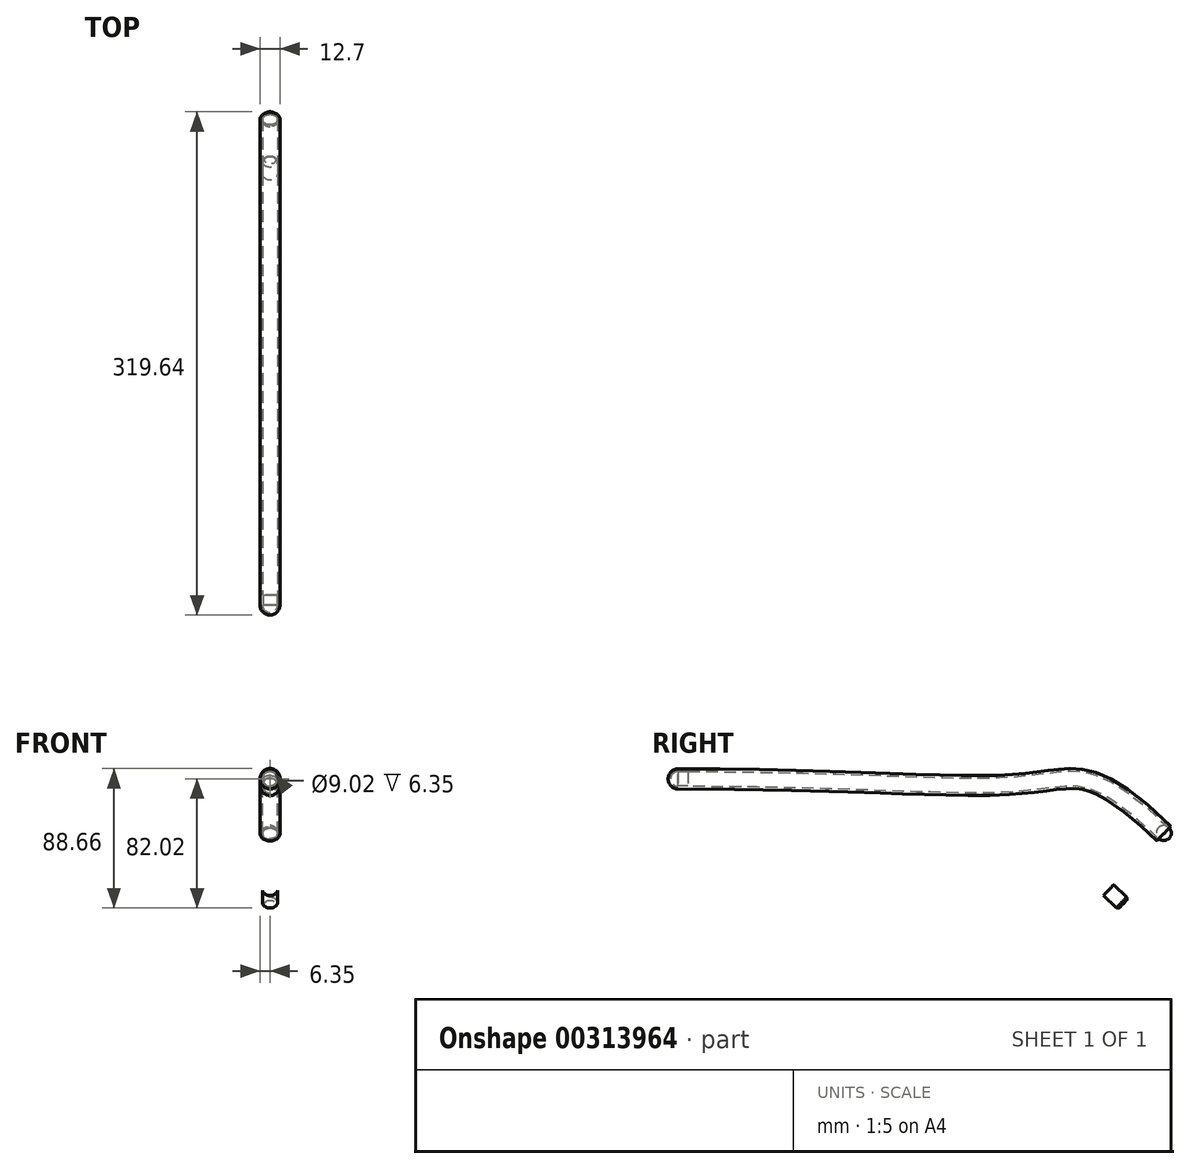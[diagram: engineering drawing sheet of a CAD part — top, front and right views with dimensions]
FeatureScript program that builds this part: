
annotation { "Feature Type Name" : "Feature", "Feature Type Description" : "" }
export const myFeature = defineFeature(function(context is Context, id is Id, definition is map)
    precondition{}
    {
        {
            var Q0;
            Q0=qCreatedBy(makeId("Right.planeOp"),FACE);
            var sketch = newSketch(context, id + "F0", { "sketchPlane" : qUnion([Q0])});
            skFitSpline(sketch, "E0", {"points": [v(-207.12, 0) * mm, v(0, -3.78) * mm, v(36.76, 0) * mm, v(101.4, -34.75) * mm], "startDerivative": vector(633.88, 0) * mm, "endDerivative": vector(361.52, -353.38) * mm});
            skPoint(sketch, "E1.0", {"position": v(0, 0) * mm});
            skFitSpline(sketch, "E2", {"points": [v(-207.12, 0) * mm, v(0, -3.78) * mm, v(36.76, 0) * mm, v(101.4, -34.75) * mm], "startDerivative": vector(633.88, 0) * mm, "endDerivative": vector(361.52, -353.38) * mm});
            skSolve(sketch);
        }
        {
            var Q0;
            Q0=sQuery(id+"F0.wireOp",VERTEX,"E0.start");
            var Q1;
            Q1=sQuery(id+"F0.wireOp",EDGE,"E0");
            cPlane(context, id + "F1", {"entities" : qUnion([Q0, Q1]), "cplaneType" : CPlaneType.CURVE_POINT, "offset" : 74.17 * mm, "width" : 152.4 * mm, "height" : 152.4 * mm});
        }
        {
            var Q0;
            Q0=qCreatedBy(makeId("Front.planeOp"),FACE);
            var Q1;
            Q1=sQuery(id+"F0.wireOp",VERTEX,"E0.3.internal");
            cPlane(context, id + "F2", {"entities" : qUnion([Q0, Q1]), "cplaneType" : CPlaneType.PLANE_POINT, "offset" : 76.2 * mm, "width" : 152.4 * mm, "height" : 152.4 * mm});
        }
        {
            var Q0;
            Q0=qCreatedBy(id+"F1.planeOp",FACE);
            var sketch = newSketch(context, id + "F3", { "sketchPlane" : qUnion([Q0])});
            skCircle(sketch, "E3", {"center": v(0, 0) * mm, "radius": 6.35 * mm});
            skCircle(sketch, "E4", {"center": v(0, 0) * mm, "radius": 4.76 * mm});
            skSolve(sketch);
        }
        {
            var Q0;
            Q0=qCreatedBy(id+"F2.planeOp",FACE);
            var sketch = newSketch(context, id + "F4", { "sketchPlane" : qUnion([Q0])});
            skArc(sketch, "E5", {"start": v(4.76, -34.23) * mm, "mid": v(-0.1, -29.56) * mm, "end": v(-4.76, -34.42) * mm});
            skLineSegment(sketch, "E6", {"start": v(4.76, -34.23) * mm, "end": v(-4.76, -34.42) * mm});
            skSolve(sketch);
        }
        {
            var Q0;
            Q0=makeQuery(id+"F3.imprint","IMPRINT",FACE,{"disambiguationData":[TD([[makeQuery(id+"F3.imprint","IMPRINT",EDGE,{"derivedFrom":sQuery(id+"F3.wireOp",EDGE,"E3")}),1.0]])]});
            var Q1;
            Q1 = qSketchRegion(id + "F0", true);
            var Q2;
            Q2=sQuery(id+"F0.wireOp",EDGE,"E0");
            sweep(context, id + "F5", {"profiles" : qUnion([Q0, Q1]), "path" : qUnion([Q2])});
        }
        {
            var Q0;
            Q0=makeQuery(id+"F5.opSweep","CAP_FACE",FACE,{"disambiguationData":[OSD([sQuery(id+"F0.wireOp",VERTEX,"E0.end"),sQuery(id+"F3.wireOp",EDGE,"E3"),sQuery(id+"F3.wireOp",EDGE,"E4")])],"isStart":false});
            var Q1;
            Q1=makeQuery(id+"F5.opSweep","CAP_FACE",FACE,{"disambiguationData":[OSD([sQuery(id+"F0.wireOp",VERTEX,"E0.end"),sQuery(id+"F3.wireOp",EDGE,"E3"),sQuery(id+"F3.wireOp",EDGE,"E4")])],"isStart":false});
            var Q2;
            Q2=makeQuery(id+"F5.opSweep","CAP_FACE",FACE,{"disambiguationData":[OSD([sQuery(id+"F0.wireOp",VERTEX,"E0.end"),sQuery(id+"F3.wireOp",EDGE,"E3"),sQuery(id+"F3.wireOp",EDGE,"E4")])],"isStart":false});
            var Q3;
            Q3=makeQuery(id+"F5.opSweep","CAP_FACE",FACE,{"disambiguationData":[OSD([sQuery(id+"F0.wireOp",VERTEX,"E0.end"),sQuery(id+"F3.wireOp",EDGE,"E3"),sQuery(id+"F3.wireOp",EDGE,"E4")])],"isStart":false});
            var Q4;
            Q4=makeQuery(id+"F5.opSweep","CAP_FACE",FACE,{"disambiguationData":[OSD([sQuery(id+"F0.wireOp",VERTEX,"E0.end"),sQuery(id+"F3.wireOp",EDGE,"E3"),sQuery(id+"F3.wireOp",EDGE,"E4")])],"isStart":false});
            var Q5;
            Q5=sQuery(id+"F0.wireOp",EDGE,"E2");
            var Q6;
            Q6=sQuery(id+"F0.wireOp",EDGE,"E2");
            var Q7;
            Q7=sQuery(id+"F0.wireOp",EDGE,"E2");
            var Q8;
            Q8=sQuery(id+"F0.wireOp",EDGE,"E2");
            sweep(context, id + "F6", {"profiles" : qUnion([Q0, Q1, Q2, Q3, Q4]), "path" : qUnion([Q5, Q6, Q7, Q8])});
        }
        {
            var Q0;
            Q0=makeQuery(id+"F6.opSweep","CAP_FACE",FACE,{"disambiguationData":[OSD([sQuery(id+"F0.wireOp",VERTEX,"E0.end"),sQuery(id+"F0.wireOp",VERTEX,"E2.end"),sQuery(id+"F3.wireOp",EDGE,"E3"),sQuery(id+"F3.wireOp",EDGE,"E4")])],"isStart":false});
            var sketch = newSketch(context, id + "F7", { "sketchPlane" : qUnion([Q0])});
            skLineSegment(sketch, "E7", {"start": v(3.77, 51.14) * mm, "end": v(3.77, 40.92) * mm});
            skLineSegment(sketch, "E8", {"start": v(-3.77, 51.14) * mm, "end": v(-3.77, 40.92) * mm});
            skCircle(sketch, "E9.0", {"center": v(0, 46.03) * mm, "radius": 6.35 * mm});
            skCircle(sketch, "E10.0", {"center": v(0, 46.03) * mm, "radius": 4.76 * mm});
            skLineSegment(sketch, "E11", {"start": v(0, 52.38) * mm, "end": v(0, 39.68) * mm});
            skArc(sketch, "E12", {"start": v(3.77, 51.14) * mm, "mid": v(0, 53.92) * mm, "end": v(-3.77, 51.14) * mm});
            skArc(sketch, "E13", {"start": v(-3.77, 40.92) * mm, "mid": v(0, 37.15) * mm, "end": v(3.77, 40.92) * mm});
            skSolve(sketch);
        }
        {
            var Q0;
            Q0=makeQuery(id+"F3.imprint","IMPRINT",FACE,{"disambiguationData":[TD([[makeQuery(id+"F3.imprint","IMPRINT",EDGE,{"derivedFrom":sQuery(id+"F3.wireOp",EDGE,"E3")}),1.0]])]});
            var sketch = newSketch(context, id + "F8", { "sketchPlane" : qUnion([Q0])});
            skLineSegment(sketch, "E14", {"start": v(0, 6.35) * mm, "end": v(0, 4.76) * mm});
            skPoint(sketch, "E15.0.center.orphan", {"position": v(0, 0) * mm});
            skCircle(sketch, "E16.0", {"center": v(0, 0) * mm, "radius": 4.76 * mm});
            skArc(sketch, "E17", {"start": v(0, 6.35) * mm, "mid": v(-6.35, 0) * mm, "end": v(0, -6.35) * mm});
            skArc(sketch, "E18", {"start": v(0, -6.35) * mm, "mid": v(6.35, 0) * mm, "end": v(0, 6.35) * mm});
            skLineSegment(sketch, "E19", {"start": v(0, 4.76) * mm, "end": v(0, 4.5) * mm});
            skLineSegment(sketch, "E20", {"start": v(0, -4.76) * mm, "end": v(0, -6.35) * mm});
            skLineSegment(sketch, "E21", {"start": v(0, -4.5) * mm, "end": v(0, -4.76) * mm});
            skLineSegment(sketch, "E22", {"start": v(0, 4.5) * mm, "end": v(0, -4.5) * mm});
            skArc(sketch, "E23", {"start": v(0, 4.76) * mm, "mid": v(-4.76, 0) * mm, "end": v(0, -4.76) * mm});
            skArc(sketch, "E24", {"start": v(0, -4.76) * mm, "mid": v(4.76, 0) * mm, "end": v(0, 4.76) * mm});
            skArc(sketch, "E25", {"start": v(0, 4.5) * mm, "mid": v(-4.5, 0) * mm, "end": v(0, -4.5) * mm});
            skArc(sketch, "E26", {"start": v(0, -4.5) * mm, "mid": v(4.5, 0) * mm, "end": v(0, 4.5) * mm});
            skSolve(sketch);
        }
        {
            var Q0;
            Q0=makeQuery(id+"F5.opSweep","CAP_FACE",FACE,{"disambiguationData":[OSD([sQuery(id+"F0.wireOp",VERTEX,"E0.end"),sQuery(id+"F3.wireOp",EDGE,"E3"),sQuery(id+"F3.wireOp",EDGE,"E4")])],"isStart":false});
            var sketch = newSketch(context, id + "F9", { "sketchPlane" : qUnion([Q0])});
            skEllipse(sketch, "E27.0", {"center": v(0, -4.14) * mm, "majorRadius": 6.35 * mm, "minorRadius": 6.35 * mm, "majorAxis": v(1, 0)});
            skEllipse(sketch, "E28.0", {"center": v(0, -4.14) * mm, "majorRadius": 4.76 * mm, "minorRadius": 4.76 * mm, "majorAxis": v(1, 0)});
            skSolve(sketch);
        }
        {
            var Q0;
            {var subQ1=sQuery(id+"F7.wireOp",EDGE,"E7");var subQ3=sQuery(id+"F7.wireOp",EDGE,"E10.0");var subQ4=makeQuery(id+"F7.imprint","INTERSECT",VERTEX,{"disambiguationData":[OD(0.0)],"derivedFrom":[subQ1,subQ3]});Q0=makeQuery(id+"F7.imprint","IMPRINT",FACE,{"disambiguationData":[TD([[makeQuery(id+"F7.imprint","IMPRINT",EDGE,{"disambiguationData":[TD([[subQ4,-1.0]])],"derivedFrom":subQ3}),-1.0]])]});}
            var Q1;
            {var subQ1=sQuery(id+"F7.wireOp",EDGE,"E7");var subQ3=sQuery(id+"F7.wireOp",EDGE,"E10.0");var subQ4=makeQuery(id+"F7.imprint","INTERSECT",VERTEX,{"disambiguationData":[OD(1.0)],"derivedFrom":[subQ1,subQ3]});Q1=makeQuery(id+"F7.imprint","IMPRINT",FACE,{"disambiguationData":[TD([[makeQuery(id+"F7.imprint","IMPRINT",EDGE,{"disambiguationData":[TD([[subQ4,1.0]])],"derivedFrom":subQ3}),-1.0]])]});}
            var Q2;
            {var subQ1=sQuery(id+"F7.wireOp",EDGE,"E8");var subQ3=sQuery(id+"F7.wireOp",EDGE,"E10.0");var subQ4=makeQuery(id+"F7.imprint","INTERSECT",VERTEX,{"disambiguationData":[OD(1.0)],"derivedFrom":[subQ1,subQ3]});Q2=makeQuery(id+"F7.imprint","IMPRINT",FACE,{"disambiguationData":[TD([[makeQuery(id+"F7.imprint","IMPRINT",EDGE,{"disambiguationData":[TD([[subQ4,-1.0]])],"derivedFrom":subQ3}),-1.0]])]});}
            var Q3;
            {var subQ0=sQuery(id+"F7.wireOp",EDGE,"E13");Q3=makeQuery(id+"F7.imprint","IMPRINT",FACE,{"disambiguationData":[TD([[makeQuery(id+"F7.imprint","IMPRINT",EDGE,{"derivedFrom":subQ0}),1.0]])]});}
            var Q4;
            {var subQ1=sQuery(id+"F7.wireOp",EDGE,"E8");var subQ3=sQuery(id+"F7.wireOp",EDGE,"E10.0");var subQ4=makeQuery(id+"F7.imprint","INTERSECT",VERTEX,{"disambiguationData":[OD(0.0)],"derivedFrom":[subQ1,subQ3]});Q4=makeQuery(id+"F7.imprint","IMPRINT",FACE,{"disambiguationData":[TD([[makeQuery(id+"F7.imprint","IMPRINT",EDGE,{"disambiguationData":[TD([[subQ4,1.0]])],"derivedFrom":subQ3}),-1.0]])]});}
            var Q5;
            {var subQ0=sQuery(id+"F7.wireOp",EDGE,"E12");Q5=makeQuery(id+"F7.imprint","IMPRINT",FACE,{"disambiguationData":[TD([[makeQuery(id+"F7.imprint","IMPRINT",EDGE,{"derivedFrom":subQ0}),1.0]])]});}
            var Q6;
            {var subQ0=sQuery(id+"F7.wireOp",EDGE,"E10.0");var subQ1=sQuery(id+"F7.wireOp",EDGE,"E7");var subQ2=makeQuery(id+"F7.imprint","INTERSECT",VERTEX,{"disambiguationData":[OD(0.0)],"derivedFrom":[subQ1,subQ0]});Q6=makeQuery(id+"F7.imprint","IMPRINT",FACE,{"disambiguationData":[TD([[makeQuery(id+"F7.imprint","IMPRINT",EDGE,{"disambiguationData":[TD([[subQ2,-1.0]])],"derivedFrom":subQ1}),-1.0]])]});}
            var Q7;
            {var subQ0=sQuery(id+"F7.wireOp",EDGE,"E10.0");var subQ1=sQuery(id+"F7.wireOp",EDGE,"E8");var subQ2=makeQuery(id+"F7.imprint","INTERSECT",VERTEX,{"disambiguationData":[OD(0.0)],"derivedFrom":[subQ1,subQ0]});Q7=makeQuery(id+"F7.imprint","IMPRINT",FACE,{"disambiguationData":[TD([[makeQuery(id+"F7.imprint","IMPRINT",EDGE,{"disambiguationData":[TD([[subQ2,-1.0]])],"derivedFrom":subQ1}),1.0]])]});}
            extrude(context, id + "F10", {"entities" : qUnion([Q0, Q1, Q2, Q3, Q4, Q5, Q6, Q7]), "operationType" : NewBodyOperationType.REMOVE, "oppositeDirection" : true, "depth" : 6.35 * mm, "offsetDistance" : 25.4 * mm});
        }
        {
            var Q0;
            {var subQ0=sQuery(id+"F8.wireOp",EDGE,"ec704d3f-fded-48ad-8db1-3264e7b653a9.0");var subQ1=sQuery(id+"F8.wireOp",EDGE,"E14");var subQ2=makeQuery(id+"F8.imprint","INTERSECT",VERTEX,{"disambiguationData":[OD(0.0)],"derivedFrom":[subQ1,subQ0]});Q0=makeQuery(id+"F8.imprint","IMPRINT",FACE,{"disambiguationData":[TD([[makeQuery(id+"F8.imprint","IMPRINT",EDGE,{"disambiguationData":[TD([[subQ2,-1.0]])],"derivedFrom":subQ1}),1.0]])]});}
            var Q1;
            Q1=sQuery(id+"F8.wireOp",EDGE,"E14");
            revolve(context, id + "F11", {"entities" : qUnion([Q0]), "axis" : qUnion([Q1]), "revolveType" : RevolveType.ONE_DIRECTION, "oppositeDirection" : true, "angle" : 180 * degree});
        }
        {
            var Q0;
            Q0=makeQuery(id+"F4.imprint","IMPRINT",FACE,{"disambiguationData":[TD([[makeQuery(id+"F4.imprint","IMPRINT",EDGE,{"derivedFrom":sQuery(id+"F4.wireOp",EDGE,"E5")}),1.0]])]});
            var Q1;
            Q1=sQuery(id+"F4.wireOp",EDGE,"E6");
            revolve(context, id + "F12", {"entities" : qUnion([Q0]), "axis" : qUnion([Q1]), "revolveType" : RevolveType.FULL});
        }
        {
            var Q0;
            {var subQ0=sQuery(id+"F3.wireOp",EDGE,"E3");var subQ1=sQuery(id+"F0.wireOp",VERTEX,"E2.end");var subQ2=sQuery(id+"F0.wireOp",VERTEX,"E0.end");Q0=makeQuery(id+"F10.boolean.opBoolean","SPLIT",EDGE,{"disambiguationData":[TD([makeQuery(id+"F10.opExtrude","SWEPT_FACE",FACE,{"disambiguationData":[OSD([sQuery(id+"F7.wireOp",EDGE,"E8")])]})])],"derivedFrom":makeQuery(id+"F6.opSweep","CAP_EDGE",EDGE,{"disambiguationData":[OSD([subQ2,subQ1,subQ0])],"isStart":false})});}
            var Q1;
            {var subQ0=sQuery(id+"F3.wireOp",EDGE,"E3");var subQ1=sQuery(id+"F0.wireOp",VERTEX,"E2.end");var subQ2=sQuery(id+"F0.wireOp",VERTEX,"E0.end");Q1=makeQuery(id+"F10.boolean.opBoolean","SPLIT",EDGE,{"disambiguationData":[TD([makeQuery(id+"F10.opExtrude","SWEPT_FACE",FACE,{"disambiguationData":[OSD([sQuery(id+"F7.wireOp",EDGE,"E7")])]})])],"derivedFrom":makeQuery(id+"F6.opSweep","CAP_EDGE",EDGE,{"disambiguationData":[OSD([subQ2,subQ1,subQ0])],"isStart":false})});}
            var Q2;
            Q2=makeQuery(id+"F10.boolean.opBoolean","INTERSECT",EDGE,{"disambiguationData":[OD(1.0)],"derivedFrom":[makeQuery(id+"F6.opSweep","SWEPT_FACE",FACE,{"disambiguationData":[OSD([sQuery(id+"F0.wireOp",VERTEX,"E0.end"),sQuery(id+"F0.wireOp",EDGE,"E2"),sQuery(id+"F3.wireOp",EDGE,"E3")])]}),makeQuery(id+"F10.opExtrude","CAP_FACE",FACE,{"disambiguationData":[OSD([sQuery(id+"F7.wireOp",EDGE,"E7"),sQuery(id+"F7.wireOp",EDGE,"E8"),sQuery(id+"F7.wireOp",EDGE,"E12"),sQuery(id+"F7.wireOp",EDGE,"E13")])],"isStart":false})]});
            var Q3;
            Q3=makeQuery(id+"F10.boolean.opBoolean","INTERSECT",EDGE,{"disambiguationData":[OD(0.0)],"derivedFrom":[makeQuery(id+"F6.opSweep","SWEPT_FACE",FACE,{"disambiguationData":[OSD([sQuery(id+"F0.wireOp",VERTEX,"E0.end"),sQuery(id+"F0.wireOp",EDGE,"E2"),sQuery(id+"F3.wireOp",EDGE,"E3")])]}),makeQuery(id+"F10.opExtrude","CAP_FACE",FACE,{"disambiguationData":[OSD([sQuery(id+"F7.wireOp",EDGE,"E7"),sQuery(id+"F7.wireOp",EDGE,"E8"),sQuery(id+"F7.wireOp",EDGE,"E12"),sQuery(id+"F7.wireOp",EDGE,"E13")])],"isStart":false})]});
            fillet(context, id + "F13", {"entities" : qUnion([Q0, Q1, Q2, Q3]), "radius" : 3.8 * mm, "tangentPropagation" : true, "allowEdgeOverflow" : false});
        }
        {
            var Q0;
            {var subQ0=sQuery(id+"F8.wireOp",EDGE,"E19");Q0=makeQuery(id+"F8.imprint","IMPRINT",FACE,{"disambiguationData":[TD([[makeQuery(id+"F8.imprint","IMPRINT",EDGE,{"derivedFrom":subQ0}),-1.0]])]});}
            var Q1;
            {var subQ0=sQuery(id+"F8.wireOp",EDGE,"E19");Q1=makeQuery(id+"F8.imprint","IMPRINT",FACE,{"disambiguationData":[TD([[makeQuery(id+"F8.imprint","IMPRINT",EDGE,{"derivedFrom":subQ0}),1.0]])]});}
            extrude(context, id + "F14", {"entities" : qUnion([Q0, Q1]), "operationType" : NewBodyOperationType.ADD, "depth" : 6.35 * mm, "offsetDistance" : 25.4 * mm});
        }
        {
            var Q0;
            {var subQ0=sQuery(id+"F9.wireOp",EDGE,"E28.0");var subQ1=makeQuery(id+"F5.opSweep","CAP_EDGE",EDGE,{"disambiguationData":[OSD([sQuery(id+"F0.wireOp",VERTEX,"E0.end"),sQuery(id+"F3.wireOp",EDGE,"E4")])],"isStart":false});var subQ2=makeQuery(id+"F9.imprint","INTERSECT",VERTEX,{"disambiguationData":[OD(0.0)],"derivedFrom":[subQ1,subQ0]});Q0=makeQuery(id+"F9.imprint","IMPRINT",FACE,{"disambiguationData":[TD([[makeQuery(id+"F9.imprint","IMPRINT",EDGE,{"disambiguationData":[TD([[subQ2,-1.0]])],"derivedFrom":subQ0}),1.0]])]});}
            extrude(context, id + "F15", {"entities" : qUnion([Q0]), "operationType" : NewBodyOperationType.ADD, "depth" : 12.7 * mm, "offsetDistance" : 25.4 * mm});
        }
        {
            var Q0;
            Q0=makeQuery(id+"F5.opSweep","CAP_EDGE",EDGE,{"disambiguationData":[OSD([sQuery(id+"F0.wireOp",VERTEX,"E0.end"),sQuery(id+"F3.wireOp",EDGE,"E4")])],"isStart":false});
            var Q1;
            {var subQ0=sQuery(id+"F3.wireOp",EDGE,"E4");var subQ1=sQuery(id+"F0.wireOp",EDGE,"E2");var subQ2=sQuery(id+"F0.wireOp",VERTEX,"E0.end");var subQ3=sQuery(id+"F3.wireOp",EDGE,"E3");var subQ4=sQuery(id+"F0.wireOp",VERTEX,"E2.end");Q1=makeQuery(id+"F13.opFillet","BLEND_EDGE",EDGE,{"blendedFrom":[makeQuery(id+"F10.boolean.opBoolean","SPLIT",EDGE,{"disambiguationData":[TD([makeQuery(id+"F10.opExtrude","SWEPT_FACE",FACE,{"disambiguationData":[OSD([sQuery(id+"F7.wireOp",EDGE,"E7")])]})])],"derivedFrom":makeQuery(id+"F6.opSweep","CAP_EDGE",EDGE,{"disambiguationData":[OSD([subQ2,subQ4,subQ3])],"isStart":false})}),makeQuery(id+"F6.opSweep","SWEPT_FACE",FACE,{"disambiguationData":[OSD([subQ2,subQ1,subQ0])]})],"blendedInto":[makeQuery(id+"F6.opSweep","SWEPT_FACE",FACE,{"disambiguationData":[OSD([subQ2,subQ1,subQ0])]})]});}
            var Q2;
            {var subQ0=sQuery(id+"F3.wireOp",EDGE,"E4");var subQ1=sQuery(id+"F0.wireOp",EDGE,"E2");var subQ2=sQuery(id+"F0.wireOp",VERTEX,"E0.end");var subQ3=sQuery(id+"F3.wireOp",EDGE,"E3");var subQ4=sQuery(id+"F0.wireOp",VERTEX,"E2.end");Q2=makeQuery(id+"F13.opFillet","BLEND_EDGE",EDGE,{"blendedFrom":[makeQuery(id+"F10.boolean.opBoolean","SPLIT",EDGE,{"disambiguationData":[TD([makeQuery(id+"F10.opExtrude","SWEPT_FACE",FACE,{"disambiguationData":[OSD([sQuery(id+"F7.wireOp",EDGE,"E8")])]})])],"derivedFrom":makeQuery(id+"F6.opSweep","CAP_EDGE",EDGE,{"disambiguationData":[OSD([subQ2,subQ4,subQ3])],"isStart":false})}),makeQuery(id+"F6.opSweep","SWEPT_FACE",FACE,{"disambiguationData":[OSD([subQ2,subQ1,subQ0])]})],"blendedInto":[makeQuery(id+"F6.opSweep","SWEPT_FACE",FACE,{"disambiguationData":[OSD([subQ2,subQ1,subQ0])]})]});}
            chamfer(context, id + "F16", {"entities" : qUnion([Q0, Q1, Q2]), "chamferType" : ChamferType.OFFSET_ANGLE, "width" : 0.25 * mm, "oppositeDirection" : false, "angle" : 30 * degree, "tangentPropagation" : true});
        }
        {
            var Q0;
            Q0=makeQuery(id+"F15.opExtrude","CAP_EDGE",EDGE,{"disambiguationData":[OSD([sQuery(id+"F9.wireOp",EDGE,"E28.0")])],"isStart":false});
            chamfer(context, id + "F17", {"entities" : qUnion([Q0]), "width" : 1.27 * mm, "tangentPropagation" : true});
        }
    });
